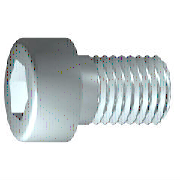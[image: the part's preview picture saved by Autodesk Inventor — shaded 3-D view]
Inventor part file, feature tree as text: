
AUTODESK INVENTOR PART (.ipt)
format: ipt  version: 2011 SP1 (Build 150282100, 282)  size: 194,048 bytes
history: native  units: mm (DEFAULTED — no unit token found)
features: extrude x1, plane x1
ambient origin geometry x7: Origin, YZ Plane, XY Plane, X Axis, Y Axis, Z Axis, Center Point
bodies: Solid1 (feature_tree), Body (feature_tree)
feature tree (2):
  extrude  "Slot"  Depth=5.90924mm
  plane  "Work Plane1"
